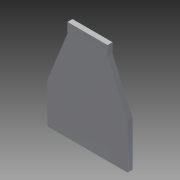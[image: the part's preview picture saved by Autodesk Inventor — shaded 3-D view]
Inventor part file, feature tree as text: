
AUTODESK INVENTOR PART (.ipt)
format: ipt  version: 2013 (Build 170138000, 138)  size: 84,480 bytes
history: native  units: in
note: dims shown in document units (in); Inventor stores cm internally (conversion verified against a paired STEP export)
features: extrude x2, sketch x2
ambient origin geometry x8: Origin, YZ Plane, XZ Plane, XY Plane, X Axis, Y Axis, Z Axis, Center Point
bodies: Solid1 (feature_tree)
feature tree (4):
  extrude  "Extrusion1"  Depth=2.25in
  extrude  "Extrusion2"  Depth=0.5in
  sketch  "Sketch1"  dims[d0=2.0in d1=2.25in]
  sketch  "Sketch2"  dims[d2=1.0in d3=0.5in d4=0.5in d5=0.125in d6=0.0in d7=0.25in d8=0.125in d9=0.0in]
